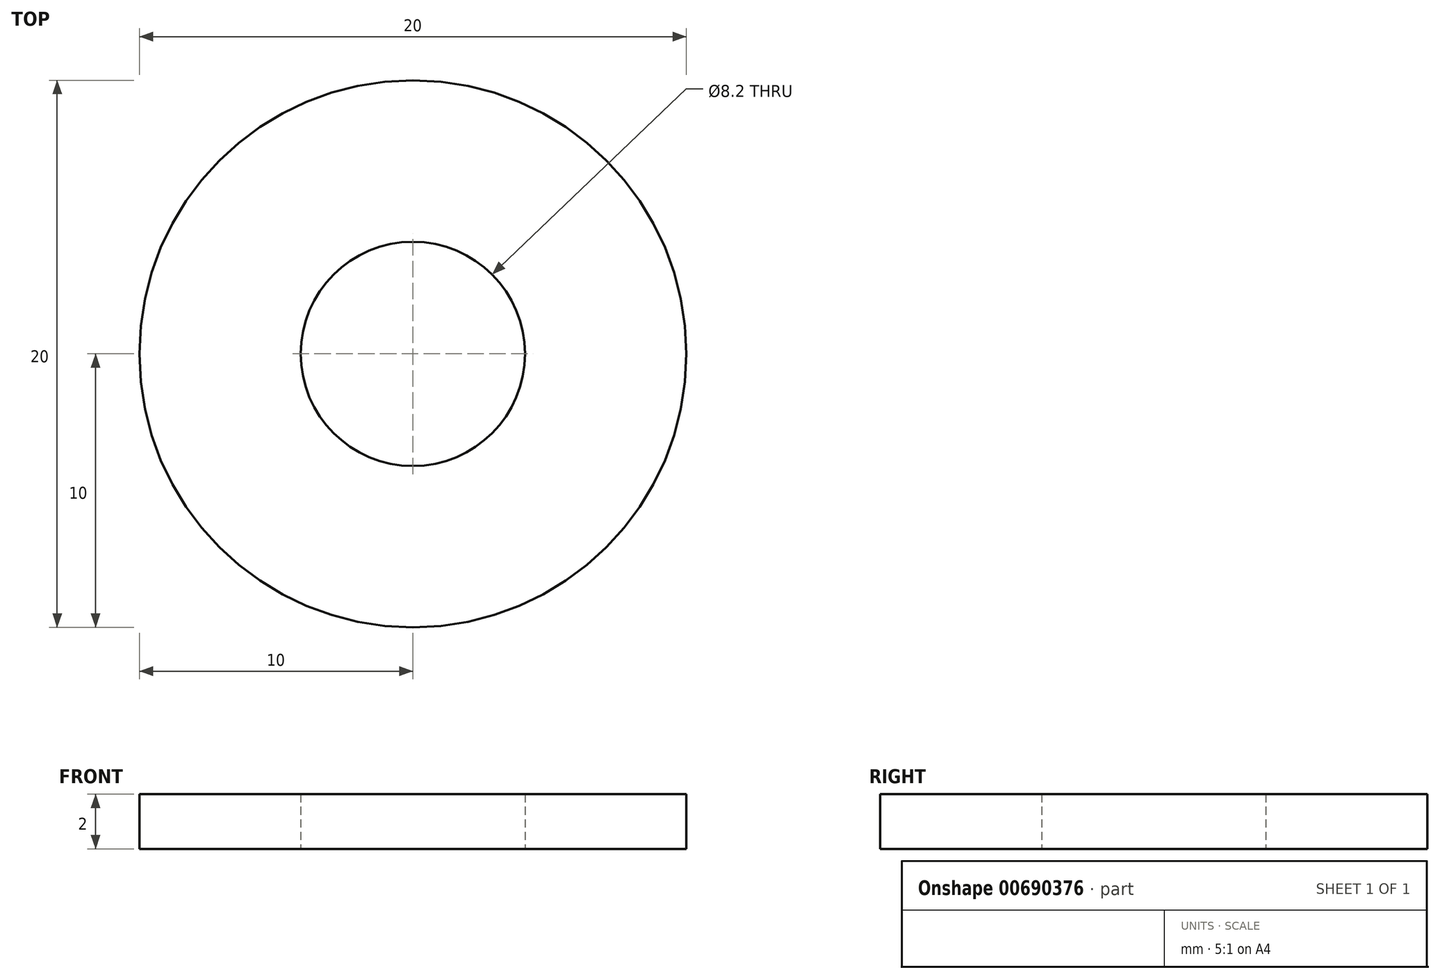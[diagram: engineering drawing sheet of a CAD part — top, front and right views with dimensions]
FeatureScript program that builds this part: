
annotation { "Feature Type Name" : "Feature", "Feature Type Description" : "" }
export const myFeature = defineFeature(function(context is Context, id is Id, definition is map)
    precondition{}
    {
        {
            var Q0;
            Q0=qCreatedBy(makeId("Top.planeOp"),FACE);
            var sketch = newSketch(context, id + "F0", { "sketchPlane" : qUnion([Q0])});
            skCircle(sketch, "E0", {"center": v(0, 0) * mm, "radius": 10 * mm});
            skCircle(sketch, "E1", {"center": v(0, 0) * mm, "radius": 4.1 * mm});
            skSolve(sketch);
        }
        {
            var Q0;
            Q0=makeQuery(id+"F0.imprint","IMPRINT",FACE,{"disambiguationData":[TD([[makeQuery(id+"F0.imprint","IMPRINT",EDGE,{"derivedFrom":sQuery(id+"F0.wireOp",EDGE,"E0")}),1.0]])]});
            extrude(context, id + "F1", {"entities" : qUnion([Q0]), "depth" : 2 * mm, "offsetDistance" : 25 * mm});
        }
    });
